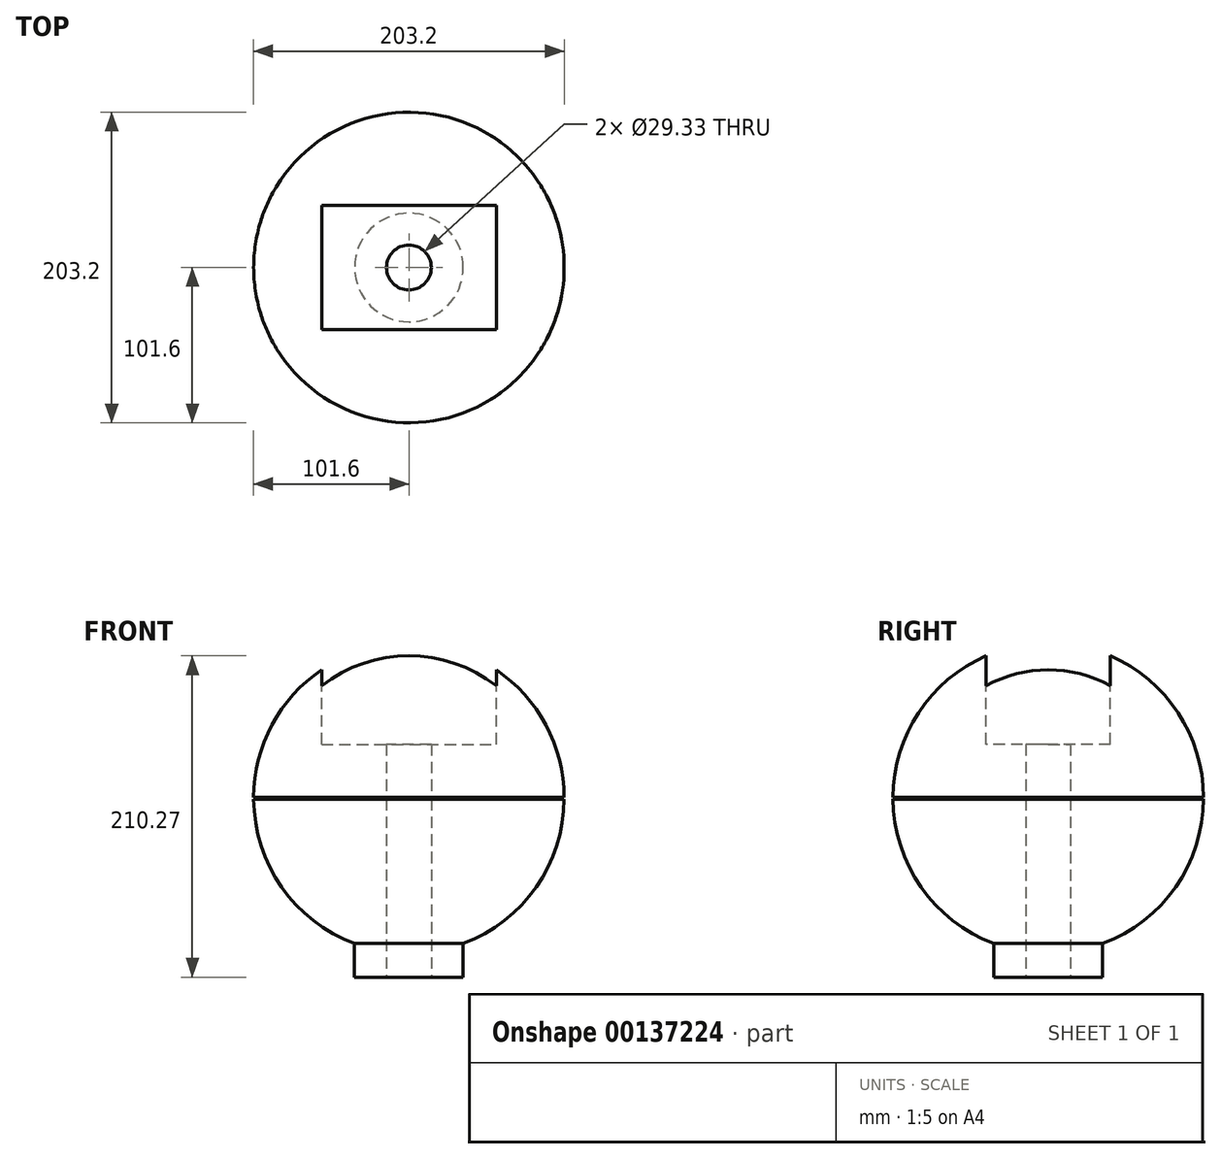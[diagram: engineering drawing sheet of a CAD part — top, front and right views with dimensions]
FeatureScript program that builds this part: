
annotation { "Feature Type Name" : "Feature", "Feature Type Description" : "" }
export const myFeature = defineFeature(function(context is Context, id is Id, definition is map)
    precondition{}
    {
        {
            var Q0;
            Q0=qCreatedBy(makeId("Top.planeOp"),FACE);
            var sketch = newSketch(context, id + "F0", { "sketchPlane" : qUnion([Q0])});
            skCircle(sketch, "E0", {"center": v(0, 0) * mm, "radius": 101.6 * mm});
            skLineSegment(sketch, "E1.bottom", {"start": v(-57.15, 40.64) * mm, "end": v(57.15, 40.64) * mm});
            skLineSegment(sketch, "E1.top", {"start": v(-57.15, -40.64) * mm, "end": v(57.15, -40.64) * mm});
            skLineSegment(sketch, "E1.left", {"start": v(-57.15, 40.64) * mm, "end": v(-57.15, -40.64) * mm});
            skLineSegment(sketch, "E1.right", {"start": v(57.15, 40.64) * mm, "end": v(57.15, -40.64) * mm});
            skPoint(sketch, "E2.middle", {"position": v(0, -40.64) * mm});
            skPoint(sketch, "E2.top.end.orphan", {"position": v(-10.16, -81.28) * mm});
            skPoint(sketch, "E2.top.start.orphan", {"position": v(25.4, -142.24) * mm});
            skLineSegment(sketch, "E3", {"start": v(-156.43, 0) * mm, "end": v(234.75, 0) * mm});
            skPoint(sketch, "E3.startSnap0", {"position": v(-57.15, 0) * mm});
            skSolve(sketch);
        }
        {
            var Q0;
            {var subQ1=sQuery(id+"F0.wireOp",EDGE,"E1.bottom");Q0=makeQuery(id+"F0.imprint","IMPRINT",FACE,{"disambiguationData":[TD([[makeQuery(id+"F0.imprint","IMPRINT",EDGE,{"derivedFrom":subQ1}),1.0]])]});}
            var Q1;
            {var subQ1=sQuery(id+"F0.wireOp",EDGE,"E1.bottom");Q1=makeQuery(id+"F0.imprint","IMPRINT",FACE,{"disambiguationData":[TD([[makeQuery(id+"F0.imprint","IMPRINT",EDGE,{"derivedFrom":subQ1}),-1.0]])]});}
            var Q2;
            Q2=sQuery(id+"F0.wireOp",EDGE,"E3");
            revolve(context, id + "F1", {"entities" : qUnion([Q0, Q1]), "axis" : qUnion([Q2]), "revolveType" : RevolveType.FULL});
        }
        {
            var Q0;
            {var subQ0=sQuery(id+"F0.wireOp",EDGE,"E1.left");var subQ1=sQuery(id+"F0.wireOp",EDGE,"E1.top");var subQ2=makeQuery(id+"F0.imprint","INTERSECT",VERTEX,{"derivedFrom":[subQ1,subQ0]});Q0=makeQuery(id+"F0.imprint","IMPRINT",FACE,{"disambiguationData":[TD([[makeQuery(id+"F0.imprint","IMPRINT",EDGE,{"disambiguationData":[TD([[subQ2,-1.0]])],"derivedFrom":subQ1}),1.0]])]});}
            var Q1;
            {var subQ0=sQuery(id+"F0.wireOp",EDGE,"E1.right");var subQ1=sQuery(id+"F0.wireOp",EDGE,"E1.top");var subQ2=makeQuery(id+"F0.imprint","INTERSECT",VERTEX,{"derivedFrom":[subQ1,subQ0]});Q1=makeQuery(id+"F0.imprint","IMPRINT",FACE,{"disambiguationData":[TD([[makeQuery(id+"F0.imprint","IMPRINT",EDGE,{"disambiguationData":[TD([[subQ2,1.0]])],"derivedFrom":subQ1}),1.0]])]});}
            var Q2;
            {var subQ1=sQuery(id+"F0.wireOp",EDGE,"E1.bottom");Q2=makeQuery(id+"F0.imprint","IMPRINT",FACE,{"disambiguationData":[TD([[makeQuery(id+"F0.imprint","IMPRINT",EDGE,{"derivedFrom":subQ1}),-1.0]])]});}
            extrude(context, id + "F2", {"entities" : qUnion([Q0, Q1, Q2]), "operationType" : NewBodyOperationType.ADD, "depth" : 202.23 * mm});
        }
        {
            var Q0;
            Q0=makeQuery(id+"F2.opExtrude","CAP_FACE",FACE,{"disambiguationData":[OSD([sQuery(id+"F0.wireOp",EDGE,"d06ad2bb-6896-4f54-809c-1f71c22c8b9c"),sQuery(id+"F0.wireOp",EDGE,"E1.bottom"),sQuery(id+"F0.wireOp",EDGE,"E1.top"),sQuery(id+"F0.wireOp",EDGE,"E1.left"),sQuery(id+"F0.wireOp",EDGE,"E1.right"),sQuery(id+"F0.wireOp",EDGE,"E2.left"),sQuery(id+"F0.wireOp",EDGE,"E2.right"),sQuery(id+"F0.wireOp",EDGE,"E3")])],"isStart":false});
            extrude(context, id + "F3", {"entities" : qUnion([Q0]), "operationType" : NewBodyOperationType.REMOVE, "oppositeDirection" : true, "depth" : 166.98 * mm});
        }
        {
            var Q0;
            Q0=makeQuery(id+"F3.boolean.opBoolean","COPY",FACE,{"derivedFrom":makeQuery(id+"F3.opExtrude","CAP_FACE",FACE,{"disambiguationData":[OSD([sQuery(id+"F0.wireOp",EDGE,"E1.bottom"),sQuery(id+"F0.wireOp",EDGE,"E1.top"),sQuery(id+"F0.wireOp",EDGE,"E1.left"),sQuery(id+"F0.wireOp",EDGE,"E1.right")])],"isStart":false})});
            var sketch = newSketch(context, id + "F4", { "sketchPlane" : qUnion([Q0])});
            skCircle(sketch, "E4", {"center": v(0, 0) * mm, "radius": 35.56 * mm});
            skLineSegment(sketch, "E5.bottom", {"start": v(-14.32, -94.5) * mm, "end": v(14.32, -94.5) * mm});
            skLineSegment(sketch, "E5.top", {"start": v(-14.32, -27.37) * mm, "end": v(14.32, -27.37) * mm});
            skLineSegment(sketch, "E5.left", {"start": v(-14.32, -94.5) * mm, "end": v(-14.32, -27.37) * mm});
            skLineSegment(sketch, "E5.right", {"start": v(14.32, -94.5) * mm, "end": v(14.32, -27.37) * mm});
            skPoint(sketch, "E5.middle", {"position": v(0, -60.93) * mm});
            skSolve(sketch);
        }
        {
            var Q0;
            Q0=makeQuery(id+"F4.imprint","IMPRINT",FACE,{"disambiguationData":[TD([[makeQuery(id+"F4.imprint","IMPRINT",EDGE,{"derivedFrom":sQuery(id+"F4.wireOp",EDGE,"E4")}),1.0]])]});
            extrude(context, id + "F5", {"entities" : qUnion([Q0]), "operationType" : NewBodyOperationType.ADD, "oppositeDirection" : true, "depth" : 152.4 * mm});
        }
        {
            var Q0;
            Q0=makeQuery(id+"F5.opExtrude","CAP_FACE",FACE,{"disambiguationData":[OSD([sQuery(id+"F4.wireOp",EDGE,"E4")])],"isStart":false});
            var sketch = newSketch(context, id + "F6", { "sketchPlane" : qUnion([Q0])});
            skCircle(sketch, "E6", {"center": v(0, 0) * mm, "radius": 14.66 * mm});
            skSolve(sketch);
        }
        {
            var Q0;
            Q0=makeQuery(id+"F6.imprint","IMPRINT",FACE,{"disambiguationData":[TD([[makeQuery(id+"F6.imprint","IMPRINT",EDGE,{"derivedFrom":sQuery(id+"F6.wireOp",EDGE,"E6")}),1.0]])]});
            extrude(context, id + "F7", {"entities" : qUnion([Q0]), "operationType" : NewBodyOperationType.REMOVE, "oppositeDirection" : true, "depth" : 328.8 * mm});
        }
        {
            var Q0;
            Q0=qCreatedBy(makeId("Right.planeOp"),FACE);
            var sketch = newSketch(context, id + "F8", { "sketchPlane" : qUnion([Q0])});
            skLineSegment(sketch, "E7.bottom", {"start": v(-127, -0.63) * mm, "end": v(127, -0.63) * mm});
            skLineSegment(sketch, "E7.top", {"start": v(-127, 0.64) * mm, "end": v(127, 0.64) * mm});
            skLineSegment(sketch, "E7.left", {"start": v(-127, -0.63) * mm, "end": v(-127, 0.64) * mm});
            skLineSegment(sketch, "E7.right", {"start": v(127, -0.63) * mm, "end": v(127, 0.64) * mm});
            skPoint(sketch, "E7.middle", {"position": v(0, 0) * mm});
            skSolve(sketch);
        }
        {
            var Q0;
            Q0=makeQuery(id+"F8.imprint","IMPRINT",FACE,{"disambiguationData":[TD([[makeQuery(id+"F8.imprint","IMPRINT",EDGE,{"derivedFrom":sQuery(id+"F8.wireOp",EDGE,"E7.bottom")}),1.0]])]});
            extrude(context, id + "F9", {"entities" : qUnion([Q0]), "operationType" : NewBodyOperationType.REMOVE, "oppositeDirection" : true, "depth" : 127 * mm, "hasSecondDirection" : true, "secondDirectionOppositeDirection" : false, "secondDirectionDepth" : 105.4 * mm});
        }
    });
